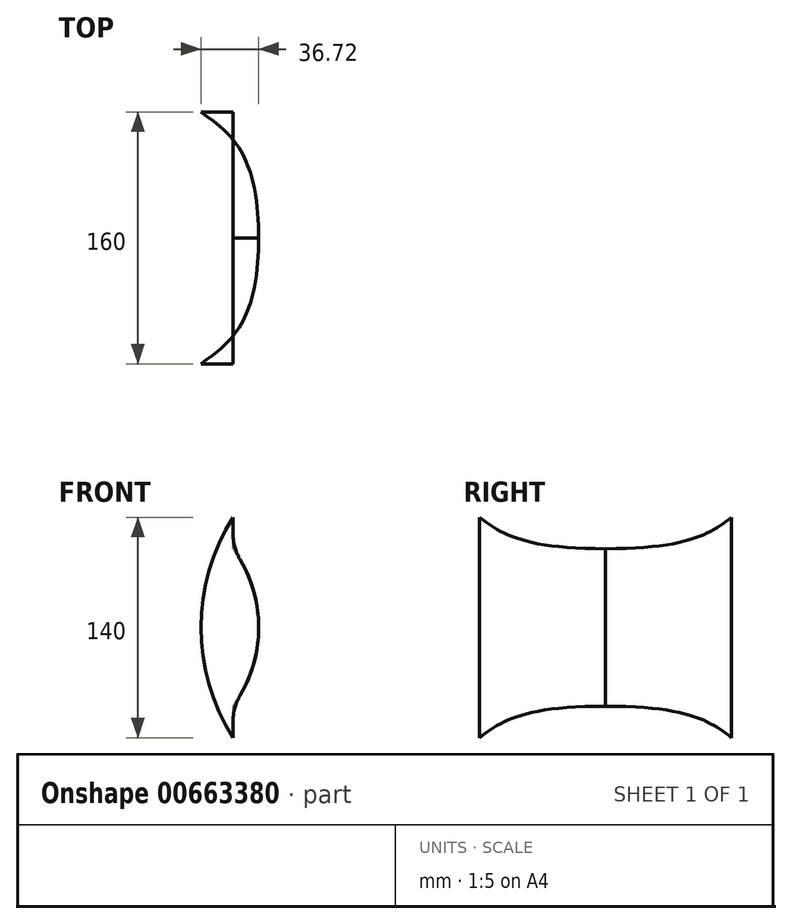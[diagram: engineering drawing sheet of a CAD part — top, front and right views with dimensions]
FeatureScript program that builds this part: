
annotation { "Feature Type Name" : "Feature", "Feature Type Description" : "" }
export const myFeature = defineFeature(function(context is Context, id is Id, definition is map)
    precondition{}
    {
        {
            var Q0;
            Q0=qCreatedBy(makeId("Front.planeOp"),FACE);
            cPlane(context, id + "F0", {"entities" : qUnion([Q0]), "cplaneType" : CPlaneType.OFFSET, "offset" : 80 * mm, "width" : 150 * mm, "height" : 150 * mm});
        }
        {
            var Q0;
            Q0=qCreatedBy(makeId("Front.planeOp"),FACE);
            var sketch = newSketch(context, id + "F1", { "sketchPlane" : qUnion([Q0])});
            skArc(sketch, "E0", {"start": v(0, -50) * mm, "mid": v(16.26, 0) * mm, "end": v(0, 50) * mm});
            skSolve(sketch);
        }
        {
            var Q0;
            Q0=qCreatedBy(id+"F0.planeOp",FACE);
            var sketch = newSketch(context, id + "F2", { "sketchPlane" : qUnion([Q0])});
            skArc(sketch, "E1", {"start": v(0, 70) * mm, "mid": v(-20.46, 0) * mm, "end": v(0, -70) * mm});
            skSolve(sketch);
        }
        {
            var Q0;
            Q0=sQuery(id+"F1.wireOp",EDGE,"E0");
            var Q1;
            Q1=sQuery(id+"F2.wireOp",EDGE,"E1");
            loft(context, id + "F3", {"bodyType" : ToolBodyType.SURFACE, "startCondition" : LoftEndDerivativeType.NORMAL_TO_PROFILE, "startMagnitude" : 2, "wireProfilesArray" : [{ "wireProfileEntities" : qUnion([Q0]) }, { "wireProfileEntities" : qUnion([Q1]) }]});
        }
        {
            var Q0;
            Q0=makeQuery(id+"F3.opLoft","SWEPT_BODY",BODY,{"disambiguationData":[OSD([sQuery(id+"F1.wireOp",EDGE,"E0"),sQuery(id+"F2.wireOp",EDGE,"E1")])]});
            var Q1;
            Q1=qCreatedBy(makeId("Front.planeOp"),FACE);
            mirror(context, id + "F4", {"entities" : qUnion([Q0]), "mirrorPlane" : qUnion([Q1])});
        }
    });
